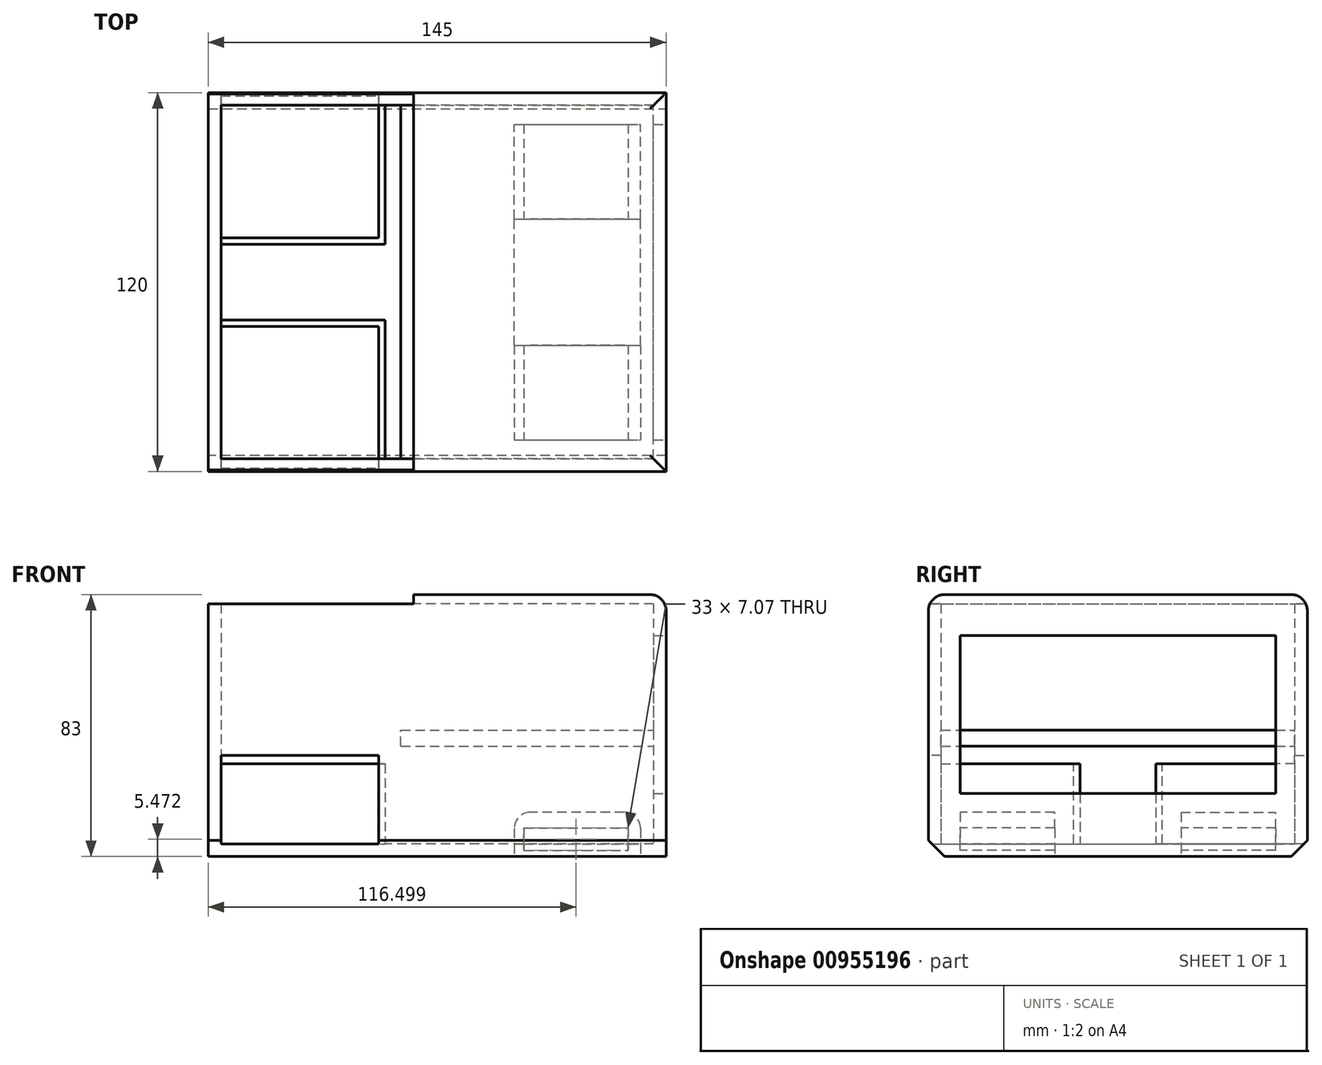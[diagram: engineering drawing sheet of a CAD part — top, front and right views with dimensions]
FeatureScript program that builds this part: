
annotation { "Feature Type Name" : "Feature", "Feature Type Description" : "" }
export const myFeature = defineFeature(function(context is Context, id is Id, definition is map)
    precondition{}
    {
        {
            var Q0;
            Q0=qCreatedBy(makeId("Top.planeOp"),FACE);
            var sketch = newSketch(context, id + "F0", { "sketchPlane" : qUnion([Q0])});
            skLineSegment(sketch, "E0.bottom", {"start": v(72.5, -60) * mm, "end": v(-72.5, -60) * mm});
            skLineSegment(sketch, "E0.top", {"start": v(72.5, 60) * mm, "end": v(-72.5, 60) * mm});
            skLineSegment(sketch, "E0.left", {"start": v(72.5, -60) * mm, "end": v(72.5, 60) * mm});
            skLineSegment(sketch, "E0.right", {"start": v(-72.5, -60) * mm, "end": v(-72.5, 60) * mm});
            skPoint(sketch, "E0.middle", {"position": v(0, 0) * mm});
            skSolve(sketch);
        }
        {
            var Q0;
            Q0=makeQuery(id+"F0.imprint","IMPRINT",FACE,{"disambiguationData":[TD([[makeQuery(id+"F0.imprint","IMPRINT",EDGE,{"derivedFrom":sQuery(id+"F0.wireOp",EDGE,"E0.bottom")}),-1.0]])]});
            extrude(context, id + "F1", {"entities" : qUnion([Q0]), "depth" : 80 * mm, "offsetDistance" : 25.4 * mm});
        }
        {
            var Q0;
            Q0=makeQuery(id+"F1.opExtrude","CAP_FACE",FACE,{"disambiguationData":[OSD([sQuery(id+"F0.wireOp",EDGE,"E0.bottom"),sQuery(id+"F0.wireOp",EDGE,"E0.top"),sQuery(id+"F0.wireOp",EDGE,"E0.left"),sQuery(id+"F0.wireOp",EDGE,"E0.right")])],"isStart":false});
            shell(context, id + "F2", {"entities" : qUnion([Q0]), "thickness" : 4 * mm});
        }
        {
            var Q0;
            Q0=makeQuery(id+"F1.opExtrude","CAP_FACE",FACE,{"disambiguationData":[OSD([sQuery(id+"F0.wireOp",EDGE,"E0.bottom"),sQuery(id+"F0.wireOp",EDGE,"E0.top"),sQuery(id+"F0.wireOp",EDGE,"E0.left"),sQuery(id+"F0.wireOp",EDGE,"E0.right")])],"isStart":true});
            var sketch = newSketch(context, id + "F3", { "sketchPlane" : qUnion([Q0])});
            skLineSegment(sketch, "E1.bottom", {"start": v(176.8, -20) * mm, "end": v(391.2, -20) * mm});
            skLineSegment(sketch, "E1.top", {"start": v(176.8, 20) * mm, "end": v(391.2, 20) * mm});
            skLineSegment(sketch, "E1.left", {"start": v(176.8, -20) * mm, "end": v(176.8, 20) * mm});
            skLineSegment(sketch, "E1.right", {"start": v(391.2, -20) * mm, "end": v(391.2, 20) * mm});
            skPoint(sketch, "E1.middle", {"position": v(284, 0) * mm});
            skLineSegment(sketch, "E2.bottom", {"start": v(24.4, -20) * mm, "end": v(64.4, -20) * mm});
            skLineSegment(sketch, "E2.top", {"start": v(24.4, 20) * mm, "end": v(64.4, 20) * mm});
            skLineSegment(sketch, "E2.left", {"start": v(24.4, -20) * mm, "end": v(24.4, 20) * mm});
            skLineSegment(sketch, "E2.right", {"start": v(64.4, -20) * mm, "end": v(64.4, 20) * mm});
            skPoint(sketch, "E2.middle", {"position": v(44.4, 0) * mm});
            skSolve(sketch);
        }
        {
            var Q0;
            Q0=makeQuery(id+"F3.imprint","IMPRINT",FACE,{"disambiguationData":[TD([[makeQuery(id+"F3.imprint","IMPRINT",EDGE,{"derivedFrom":sQuery(id+"F3.wireOp",EDGE,"E2.bottom")}),1.0]])]});
            extrude(context, id + "F4", {"entities" : qUnion([Q0]), "operationType" : NewBodyOperationType.REMOVE, "oppositeDirection" : true, "depth" : 25.4 * mm, "offsetDistance" : 25.4 * mm});
        }
        {
            var Q0;
            Q0=makeQuery(id+"F2.opShell","OFFSET_FACE",FACE,{"disambiguationData":[OSD([sQuery(id+"F0.wireOp",EDGE,"E0.bottom"),sQuery(id+"F0.wireOp",EDGE,"E0.top"),sQuery(id+"F0.wireOp",EDGE,"E0.left"),sQuery(id+"F0.wireOp",EDGE,"E0.right")])]});
            var sketch = newSketch(context, id + "F5", { "sketchPlane" : qUnion([Q0])});
            skLineSegment(sketch, "E3.bottom", {"start": v(24.4, 20) * mm, "end": v(64.4, 20) * mm});
            skLineSegment(sketch, "E3.top", {"start": v(24.4, 50) * mm, "end": v(64.4, 50) * mm});
            skLineSegment(sketch, "E3.left", {"start": v(24.4, 20) * mm, "end": v(24.4, 50) * mm});
            skLineSegment(sketch, "E3.right", {"start": v(64.4, 20) * mm, "end": v(64.4, 50) * mm});
            skLineSegment(sketch, "E4.bottom", {"start": v(24.4, -20) * mm, "end": v(64.4, -20) * mm});
            skLineSegment(sketch, "E4.top", {"start": v(24.4, -50) * mm, "end": v(64.4, -50) * mm});
            skLineSegment(sketch, "E4.left", {"start": v(24.4, -20) * mm, "end": v(24.4, -50) * mm});
            skLineSegment(sketch, "E4.right", {"start": v(64.4, -20) * mm, "end": v(64.4, -50) * mm});
            skSolve(sketch);
        }
        {
            var Q0;
            Q0=makeQuery(id+"F5.imprint","IMPRINT",FACE,{"disambiguationData":[TD([[makeQuery(id+"F5.imprint","IMPRINT",EDGE,{"derivedFrom":sQuery(id+"F5.wireOp",EDGE,"E3.bottom")}),-1.0]])]});
            var Q1;
            Q1=makeQuery(id+"F5.imprint","IMPRINT",FACE,{"disambiguationData":[TD([[makeQuery(id+"F5.imprint","IMPRINT",EDGE,{"derivedFrom":sQuery(id+"F5.wireOp",EDGE,"E4.bottom")}),1.0]])]});
            extrude(context, id + "F6", {"entities" : qUnion([Q0, Q1]), "operationType" : NewBodyOperationType.ADD, "depth" : 10 * mm, "offsetDistance" : 25.4 * mm});
        }
        {
            var Q0;
            Q0=makeQuery(id+"F6.opExtrude","CAP_EDGE",EDGE,{"disambiguationData":[OSD([sQuery(id+"F5.wireOp",EDGE,"E3.left")])],"isStart":false});
            var Q1;
            Q1=makeQuery(id+"F6.opExtrude","CAP_EDGE",EDGE,{"disambiguationData":[OSD([sQuery(id+"F5.wireOp",EDGE,"E3.right")])],"isStart":false});
            var Q2;
            Q2=makeQuery(id+"F6.opExtrude","CAP_EDGE",EDGE,{"disambiguationData":[OSD([sQuery(id+"F5.wireOp",EDGE,"E4.right")])],"isStart":false});
            var Q3;
            Q3=makeQuery(id+"F6.opExtrude","CAP_EDGE",EDGE,{"disambiguationData":[OSD([sQuery(id+"F5.wireOp",EDGE,"E4.left")])],"isStart":false});
            fillet(context, id + "F7", {"entities" : qUnion([Q0, Q1, Q2, Q3]), "radius" : 5.08 * mm, "tangentPropagation" : true, "allowEdgeOverflow" : false});
        }
        {
            var Q0;
            Q0=makeQuery(id+"F1.opExtrude","SWEPT_FACE",FACE,{"disambiguationData":[OSD([sQuery(id+"F0.wireOp",EDGE,"E0.left")])]});
            var sketch = newSketch(context, id + "F8", { "sketchPlane" : qUnion([Q0])});
            skLineSegment(sketch, "E5.bottom", {"start": v(50, 20) * mm, "end": v(-50, 20) * mm});
            skLineSegment(sketch, "E5.top", {"start": v(50, 70) * mm, "end": v(-50, 70) * mm});
            skLineSegment(sketch, "E5.left", {"start": v(50, 20) * mm, "end": v(50, 70) * mm});
            skLineSegment(sketch, "E5.right", {"start": v(-50, 20) * mm, "end": v(-50, 70) * mm});
            skPoint(sketch, "E5.middle", {"position": v(0, 45) * mm});
            skSolve(sketch);
        }
        {
            var Q0;
            Q0=makeQuery(id+"F8.imprint","IMPRINT",FACE,{"disambiguationData":[TD([[makeQuery(id+"F8.imprint","IMPRINT",EDGE,{"derivedFrom":sQuery(id+"F8.wireOp",EDGE,"E5.bottom")}),-1.0]])]});
            extrude(context, id + "F9", {"entities" : qUnion([Q0]), "operationType" : NewBodyOperationType.REMOVE, "oppositeDirection" : true, "depth" : 25.4 * mm, "offsetDistance" : 25.4 * mm});
        }
        {
            var Q0;
            Q0=makeQuery(id+"F2.opShell","OFFSET_FACE",FACE,{"disambiguationData":[OSD([sQuery(id+"F0.wireOp",EDGE,"E0.top")])]});
            var sketch = newSketch(context, id + "F10", { "sketchPlane" : qUnion([Q0])});
            skLineSegment(sketch, "E6.bottom", {"start": v(-11.5, 35) * mm, "end": v(68.5, 35) * mm});
            skLineSegment(sketch, "E6.top", {"start": v(-11.5, 40) * mm, "end": v(68.5, 40) * mm});
            skLineSegment(sketch, "E6.left", {"start": v(-11.5, 35) * mm, "end": v(-11.5, 40) * mm});
            skLineSegment(sketch, "E6.right", {"start": v(68.5, 35) * mm, "end": v(68.5, 40) * mm});
            skSolve(sketch);
        }
        {
            var Q0;
            Q0 = qSketchRegion(id + "F10", true);
            extrude(context, id + "F11", {"entities" : qUnion([Q0]), "operationType" : NewBodyOperationType.ADD, "depth" : 112 * mm, "offsetDistance" : 25.4 * mm});
        }
        {
            var Q0;
            Q0=qCreatedBy(makeId("Front.planeOp"),FACE);
            var sketch = newSketch(context, id + "F12", { "sketchPlane" : qUnion([Q0])});
            skLineSegment(sketch, "E7.bottom", {"start": v(60.5, 1.94) * mm, "end": v(27.5, 1.94) * mm});
            skLineSegment(sketch, "E7.top", {"start": v(60.5, 9) * mm, "end": v(27.5, 9) * mm});
            skLineSegment(sketch, "E7.left", {"start": v(60.5, 1.94) * mm, "end": v(60.5, 9) * mm});
            skLineSegment(sketch, "E7.right", {"start": v(27.5, 1.94) * mm, "end": v(27.5, 9) * mm});
            skSolve(sketch);
        }
        {
            var Q0;
            Q0 = qSketchRegion(id + "F12", true);
            extrude(context, id + "F13", {"entities" : qUnion([Q0]), "operationType" : NewBodyOperationType.REMOVE, "oppositeDirection" : true, "depth" : 50 * mm, "offsetDistance" : 25.4 * mm, "hasSecondDirection" : true, "secondDirectionOppositeDirection" : false, "secondDirectionDepth" : 50 * mm});
        }
        {
            var Q0;
            Q0=makeQuery(id+"F2.opShell","OFFSET_FACE",FACE,{"disambiguationData":[OSD([sQuery(id+"F0.wireOp",EDGE,"E0.bottom"),sQuery(id+"F0.wireOp",EDGE,"E0.top"),sQuery(id+"F0.wireOp",EDGE,"E0.left"),sQuery(id+"F0.wireOp",EDGE,"E0.right")])]});
            var sketch = newSketch(context, id + "F14", { "sketchPlane" : qUnion([Q0])});
            skLineSegment(sketch, "E8.bottom", {"start": v(-68.5, 56) * mm, "end": v(-16.5, 56) * mm});
            skLineSegment(sketch, "E8.top", {"start": v(-68.5, 12) * mm, "end": v(-16.5, 12) * mm});
            skLineSegment(sketch, "E8.left", {"start": v(-68.5, 56) * mm, "end": v(-68.5, 12) * mm});
            skLineSegment(sketch, "E8.right", {"start": v(-16.5, 56) * mm, "end": v(-16.5, 12) * mm});
            skLineSegment(sketch, "E9.bottom", {"start": v(-68.5, -56) * mm, "end": v(-16.5, -56) * mm});
            skLineSegment(sketch, "E9.top", {"start": v(-68.5, -12) * mm, "end": v(-16.5, -12) * mm});
            skLineSegment(sketch, "E9.left", {"start": v(-68.5, -56) * mm, "end": v(-68.5, -12) * mm});
            skLineSegment(sketch, "E9.right", {"start": v(-16.5, -56) * mm, "end": v(-16.5, -12) * mm});
            skSolve(sketch);
        }
        {
            var Q0;
            Q0 = qSketchRegion(id + "F14", true);
            extrude(context, id + "F15", {"entities" : qUnion([Q0]), "operationType" : NewBodyOperationType.ADD, "depth" : 25.4 * mm, "offsetDistance" : 25.4 * mm});
        }
        {
            var Q0;
            Q0=makeQuery(id+"F15.opExtrude","CAP_FACE",FACE,{"disambiguationData":[OSD([sQuery(id+"F14.wireOp",EDGE,"E9.bottom"),sQuery(id+"F14.wireOp",EDGE,"E9.top"),sQuery(id+"F14.wireOp",EDGE,"E9.left"),sQuery(id+"F14.wireOp",EDGE,"E9.right")])],"isStart":false});
            var sketch = newSketch(context, id + "F16", { "sketchPlane" : qUnion([Q0])});
            skLineSegment(sketch, "E10.bottom", {"start": v(-68.5, -56) * mm, "end": v(-18.5, -56) * mm});
            skLineSegment(sketch, "E10.top", {"start": v(-68.5, -14) * mm, "end": v(-18.5, -14) * mm});
            skLineSegment(sketch, "E10.left", {"start": v(-68.5, -56) * mm, "end": v(-68.5, -14) * mm});
            skLineSegment(sketch, "E10.right", {"start": v(-18.5, -56) * mm, "end": v(-18.5, -14) * mm});
            skPoint(sketch, "E11", {"position": v(-68.5, 56) * mm});
            skLineSegment(sketch, "E12.bottom", {"start": v(-68.5, 56) * mm, "end": v(-18.5, 56) * mm});
            skLineSegment(sketch, "E12.top", {"start": v(-68.5, 14) * mm, "end": v(-18.5, 14) * mm});
            skLineSegment(sketch, "E12.left", {"start": v(-68.5, 56) * mm, "end": v(-68.5, 14) * mm});
            skLineSegment(sketch, "E12.right", {"start": v(-18.5, 56) * mm, "end": v(-18.5, 14) * mm});
            skSolve(sketch);
        }
        {
            var Q0;
            Q0=makeQuery(id+"F16.imprint","IMPRINT",FACE,{"disambiguationData":[TD([[makeQuery(id+"F16.imprint","IMPRINT",EDGE,{"derivedFrom":sQuery(id+"F16.wireOp",EDGE,"E12.bottom")}),-1.0]])]});
            var Q1;
            Q1=makeQuery(id+"F16.imprint","IMPRINT",FACE,{"disambiguationData":[TD([[makeQuery(id+"F16.imprint","IMPRINT",EDGE,{"derivedFrom":sQuery(id+"F16.wireOp",EDGE,"E10.bottom")}),-1.0]])]});
            extrude(context, id + "F17", {"entities" : qUnion([Q0, Q1]), "operationType" : NewBodyOperationType.REMOVE, "oppositeDirection" : true, "depth" : 25.4 * mm, "offsetDistance" : 25.4 * mm});
        }
        {
            var Q0;
            Q0=makeQuery(id+"F1.opExtrude","SWEPT_FACE",FACE,{"disambiguationData":[OSD([sQuery(id+"F0.wireOp",EDGE,"E0.top")])]});
            var sketch = newSketch(context, id + "F18", { "sketchPlane" : qUnion([Q0])});
            skLineSegment(sketch, "E13.bottom", {"start": v(18.5, 32) * mm, "end": v(68.5, 32) * mm});
            skLineSegment(sketch, "E13.top", {"start": v(18.5, 4) * mm, "end": v(68.5, 4) * mm});
            skLineSegment(sketch, "E13.left", {"start": v(18.5, 32) * mm, "end": v(18.5, 4) * mm});
            skLineSegment(sketch, "E13.right", {"start": v(68.5, 32) * mm, "end": v(68.5, 4) * mm});
            skSolve(sketch);
        }
        {
            var Q0;
            Q0=makeQuery(id+"F18.imprint","IMPRINT",FACE,{"disambiguationData":[TD([[makeQuery(id+"F18.imprint","IMPRINT",EDGE,{"derivedFrom":sQuery(id+"F18.wireOp",EDGE,"E13.bottom")}),-1.0]])]});
            extrude(context, id + "F19", {"entities" : qUnion([Q0]), "operationType" : NewBodyOperationType.REMOVE, "oppositeDirection" : true, "depth" : 25.4 * mm, "offsetDistance" : 25.4 * mm});
        }
        {
            var Q0;
            Q0=makeQuery(id+"F1.opExtrude","SWEPT_FACE",FACE,{"disambiguationData":[OSD([sQuery(id+"F0.wireOp",EDGE,"E0.bottom")])]});
            var sketch = newSketch(context, id + "F20", { "sketchPlane" : qUnion([Q0])});
            skLineSegment(sketch, "E14.bottom", {"start": v(-18.5, 32) * mm, "end": v(-68.5, 32) * mm});
            skLineSegment(sketch, "E14.top", {"start": v(-18.5, 4) * mm, "end": v(-68.5, 4) * mm});
            skLineSegment(sketch, "E14.left", {"start": v(-18.5, 32) * mm, "end": v(-18.5, 4) * mm});
            skLineSegment(sketch, "E14.right", {"start": v(-68.5, 32) * mm, "end": v(-68.5, 4) * mm});
            skSolve(sketch);
        }
        {
            var Q0;
            Q0=makeQuery(id+"F20.imprint","IMPRINT",FACE,{"disambiguationData":[TD([[makeQuery(id+"F20.imprint","IMPRINT",EDGE,{"derivedFrom":sQuery(id+"F20.wireOp",EDGE,"E14.bottom")}),1.0]])]});
            extrude(context, id + "F21", {"entities" : qUnion([Q0]), "operationType" : NewBodyOperationType.REMOVE, "oppositeDirection" : true, "depth" : 25.4 * mm, "offsetDistance" : 25.4 * mm});
        }
        {
            var Q0;
            Q0=makeQuery(id+"F1.opExtrude","CAP_FACE",FACE,{"disambiguationData":[OSD([sQuery(id+"F0.wireOp",EDGE,"E0.bottom"),sQuery(id+"F0.wireOp",EDGE,"E0.top"),sQuery(id+"F0.wireOp",EDGE,"E0.left"),sQuery(id+"F0.wireOp",EDGE,"E0.right")])],"isStart":false});
            var sketch = newSketch(context, id + "F22", { "sketchPlane" : qUnion([Q0])});
            skLineSegment(sketch, "E15.bottom", {"start": v(72.5, 60) * mm, "end": v(-7.5, 60) * mm});
            skLineSegment(sketch, "E15.top", {"start": v(72.5, -60) * mm, "end": v(-7.5, -60) * mm});
            skLineSegment(sketch, "E15.left", {"start": v(72.5, 60) * mm, "end": v(72.5, -60) * mm});
            skLineSegment(sketch, "E15.right", {"start": v(-7.5, 60) * mm, "end": v(-7.5, -60) * mm});
            skSolve(sketch);
        }
        {
            var Q0;
            Q0 = qSketchRegion(id + "F22", true);
            extrude(context, id + "F23", {"entities" : qUnion([Q0]), "operationType" : NewBodyOperationType.ADD, "depth" : 3 * mm, "offsetDistance" : 25.4 * mm});
        }
        {
            var Q0;
            Q0=makeQuery(id+"F23.opExtrude","CAP_EDGE",EDGE,{"disambiguationData":[OSD([sQuery(id+"F22.wireOp",EDGE,"E15.bottom")])],"isStart":false});
            var Q1;
            Q1=makeQuery(id+"F23.opExtrude","CAP_EDGE",EDGE,{"disambiguationData":[OSD([sQuery(id+"F22.wireOp",EDGE,"E15.top")])],"isStart":false});
            var Q2;
            Q2=makeQuery(id+"F23.opExtrude","CAP_EDGE",EDGE,{"disambiguationData":[OSD([sQuery(id+"F22.wireOp",EDGE,"E15.left")])],"isStart":false});
            fillet(context, id + "F24", {"entities" : qUnion([Q0, Q1, Q2]), "radius" : 5.08 * mm, "tangentPropagation" : true, "allowEdgeOverflow" : false});
        }
        {
            var Q0;
            Q0=makeQuery(id+"F1.opExtrude","CAP_EDGE",EDGE,{"disambiguationData":[OSD([sQuery(id+"F0.wireOp",EDGE,"E0.top")])],"isStart":true});
            var Q1;
            Q1=makeQuery(id+"F1.opExtrude","CAP_EDGE",EDGE,{"disambiguationData":[OSD([sQuery(id+"F0.wireOp",EDGE,"E0.bottom")])],"isStart":true});
            chamfer(context, id + "F25", {"entities" : qUnion([Q0, Q1]), "width" : 5.08 * mm, "tangentPropagation" : true});
        }
    });
